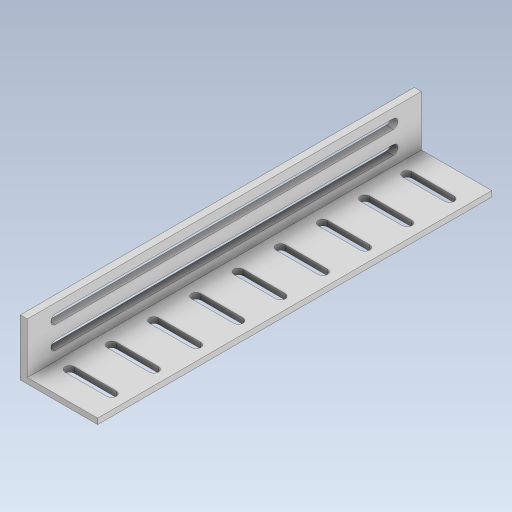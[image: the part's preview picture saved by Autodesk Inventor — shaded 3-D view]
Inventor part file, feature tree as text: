
AUTODESK INVENTOR PART (.ipt)
format: ipt  version: 2023.5 (Build 275446000, 446)  size: 431,104 bytes
history: native  units: mm
features: extrude x3, sketch x2
ambient origin geometry x8: Origin, YZ Plane, XZ Plane, XY Plane, X Axis, Y Axis, Z Axis, Center Point
bodies: Solid1 (feature_tree)
feature tree (5):
  sketch  "Sketch1"  dims[d0=27.5mm d1=140.0mm]
  extrude  "Extrusion1"  Depth=140.0mm
  extrude  "Extrusion2"  Depth=2.0mm TaperAngle=0.0deg
  extrude  "Extrusion3"  Depth=20.0mm TaperAngle=0.0deg
  sketch  "Sketch2"  dims[d2=2.5mm d3=2.0mm d4=0.0mm d5=20.0mm d6=0.0mm d7=3.3mm d8=5.0mm d9=3.3mm d10=5.0mm d11=10.0mm d12=10.0mm d15=3.3mm d16=3.3mm d17=2.5mm d18=0.0mm d19=120.0mm d20=120.0mm d21=3.3mm d22=10.0mm d23=5.0mm d24=3.3mm d25=5.0mm d26=90.0mm d28=15.0mm d29=10.0mm d31=10.0mm]
